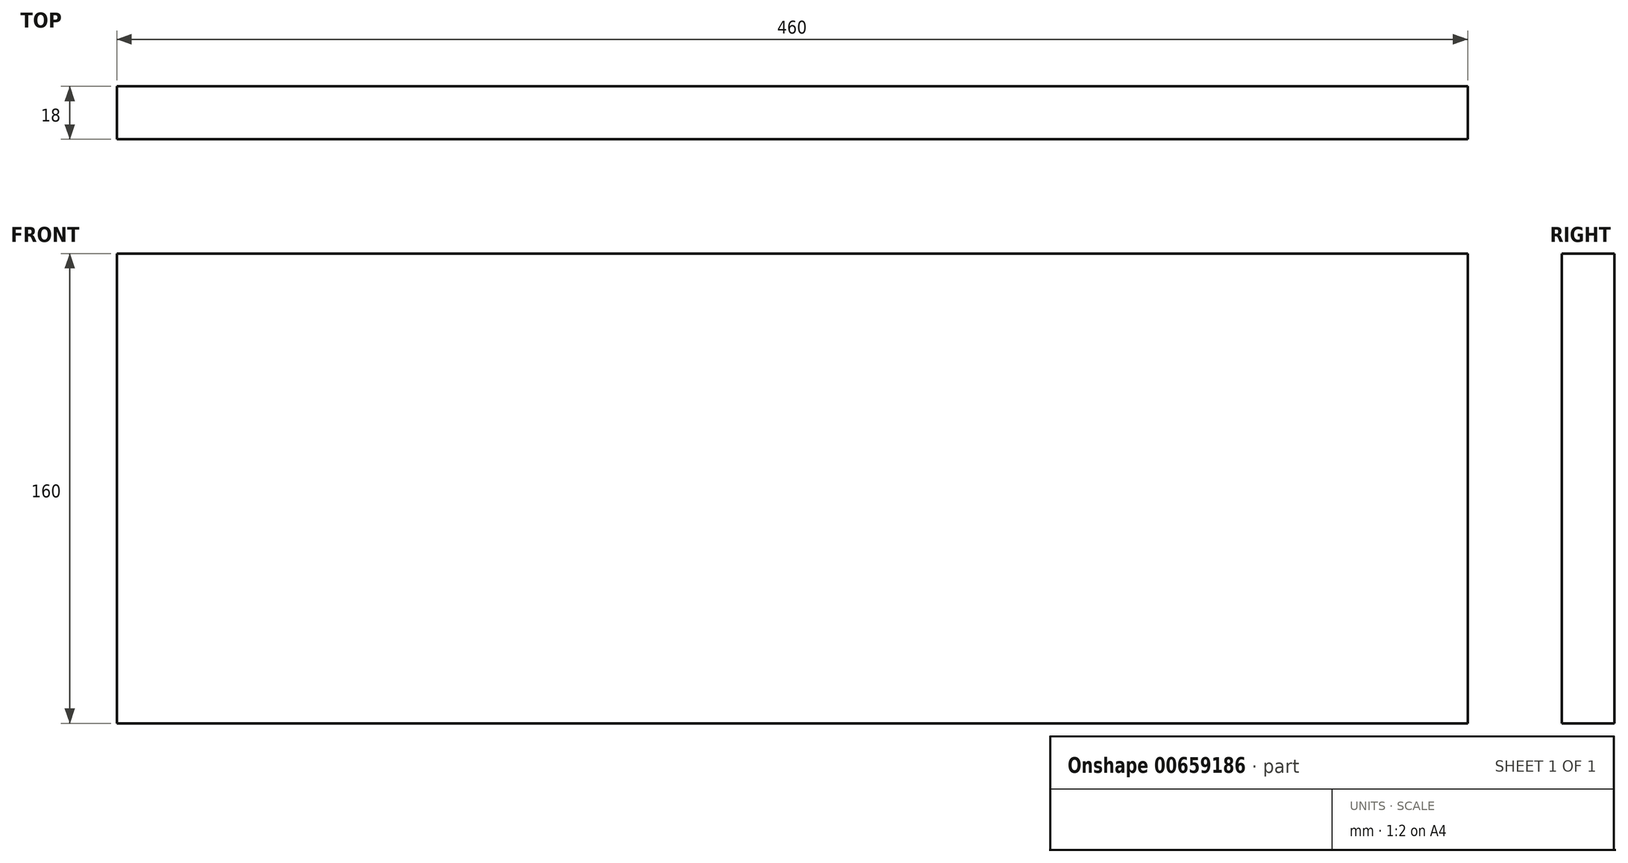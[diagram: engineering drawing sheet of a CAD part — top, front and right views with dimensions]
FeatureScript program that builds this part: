
annotation { "Feature Type Name" : "Feature", "Feature Type Description" : "" }
export const myFeature = defineFeature(function(context is Context, id is Id, definition is map)
    precondition{}
    {
        {
            var Q0;
            Q0=qCreatedBy(makeId("Front.planeOp"),FACE);
            var sketch = newSketch(context, id + "F0", { "sketchPlane" : qUnion([Q0])});
            skLineSegment(sketch, "E0.bottom", {"start": v(-214.81, 80) * mm, "end": v(245.19, 80) * mm});
            skLineSegment(sketch, "E0.top", {"start": v(-214.81, -80) * mm, "end": v(245.19, -80) * mm});
            skLineSegment(sketch, "E0.left", {"start": v(-214.81, 80) * mm, "end": v(-214.81, -80) * mm});
            skLineSegment(sketch, "E0.right", {"start": v(245.19, 80) * mm, "end": v(245.19, -80) * mm});
            skPoint(sketch, "E0.middle", {"position": v(15.19, 0) * mm});
            skSolve(sketch);
        }
        {
            var Q0;
            Q0=makeQuery(id+"F0.imprint","IMPRINT",FACE,{"disambiguationData":[TD([[makeQuery(id+"F0.imprint","IMPRINT",EDGE,{"derivedFrom":sQuery(id+"F0.wireOp",EDGE,"E0.bottom")}),-1.0]])]});
            extrude(context, id + "F1", {"entities" : qUnion([Q0]), "endBound" : BoundingType.SYMMETRIC, "depth" : 18 * mm, "offsetDistance" : 25 * mm});
        }
    });
